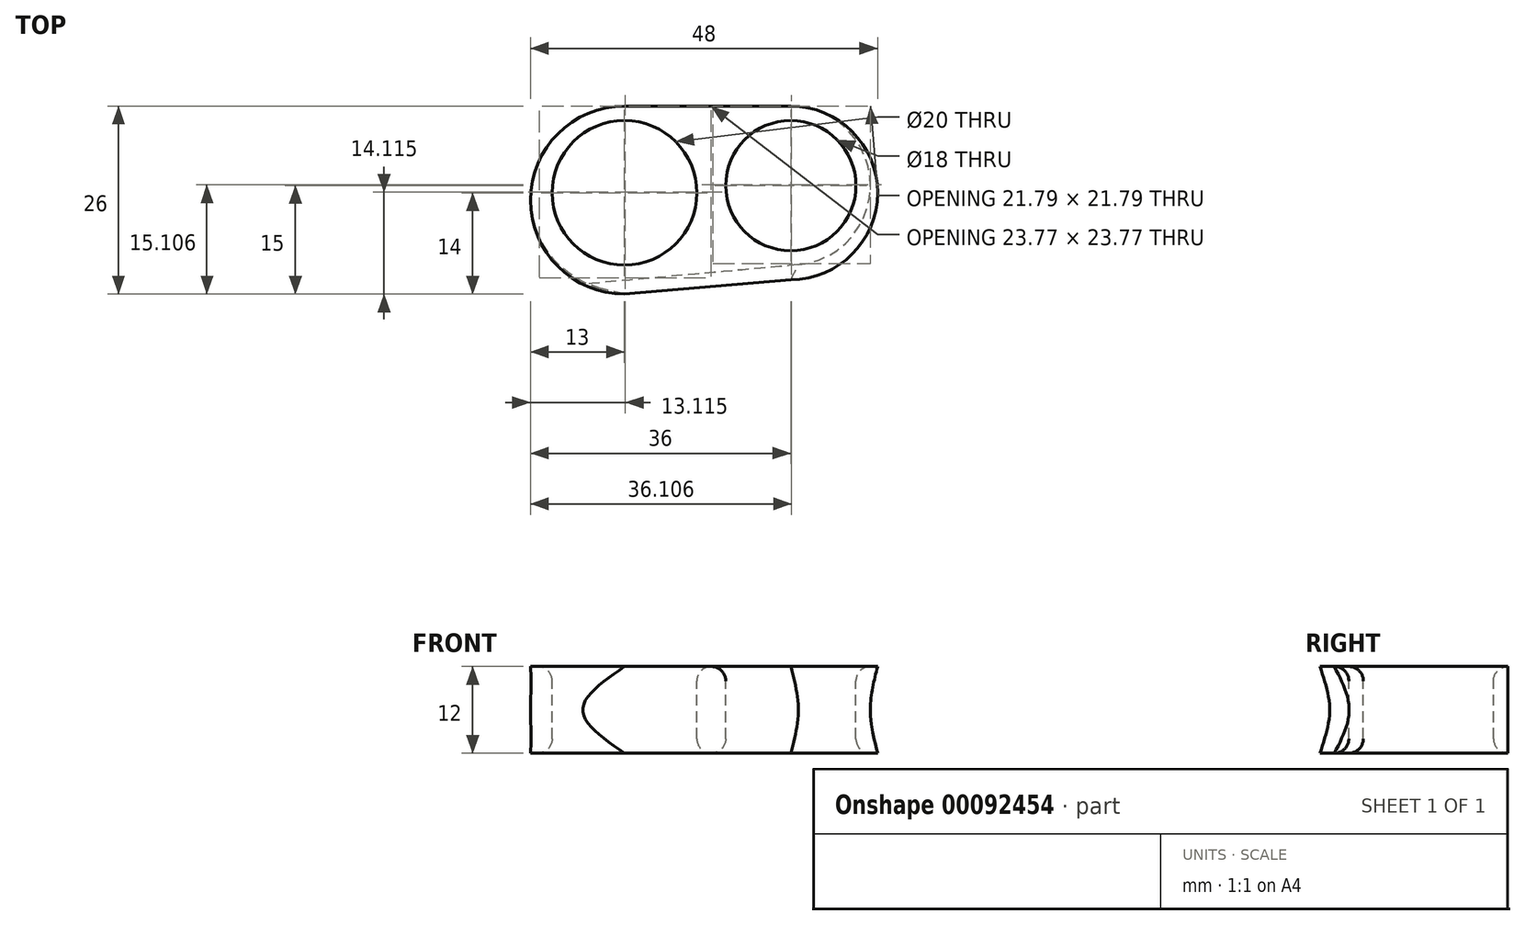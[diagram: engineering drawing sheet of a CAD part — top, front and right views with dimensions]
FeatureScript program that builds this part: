
annotation { "Feature Type Name" : "Feature", "Feature Type Description" : "" }
export const myFeature = defineFeature(function(context is Context, id is Id, definition is map)
    precondition{}
    {
        {
            var Q0;
            Q0=qCreatedBy(makeId("Top.planeOp"),FACE);
            var sketch = newSketch(context, id + "F0", { "sketchPlane" : qUnion([Q0])});
            skLineSegment(sketch, "E0.bottom", {"start": v(26, 15) * mm, "end": v(-26, 15) * mm, "construction": true});
            skLineSegment(sketch, "E0.top", {"start": v(26, -15) * mm, "end": v(-26, -15) * mm, "construction": true});
            skLineSegment(sketch, "E0.left", {"start": v(26, 15) * mm, "end": v(26, -15) * mm, "construction": true});
            skLineSegment(sketch, "E0.right", {"start": v(-26, 15) * mm, "end": v(-26, -15) * mm, "construction": true});
            skPoint(sketch, "E0.middle", {"position": v(0, 0) * mm});
            skLineSegment(sketch, "E1", {"start": v(-26, 13) * mm, "end": v(26, 13) * mm, "construction": true});
            skLineSegment(sketch, "E2", {"start": v(-22, 15) * mm, "end": v(-22, -15) * mm, "construction": true});
            skLineSegment(sketch, "E3", {"start": v(-2, 15) * mm, "end": v(-2, -15) * mm, "construction": true});
            skLineSegment(sketch, "E4", {"start": v(2, 15) * mm, "end": v(2, -15) * mm, "construction": true});
            skLineSegment(sketch, "E5", {"start": v(-24, 15) * mm, "end": v(-24, -15) * mm, "construction": true});
            skLineSegment(sketch, "E6", {"start": v(20, 15) * mm, "end": v(20, -15) * mm, "construction": true});
            skLineSegment(sketch, "E7", {"start": v(-22, -7) * mm, "end": v(-2, -7) * mm, "construction": true});
            skLineSegment(sketch, "E8", {"start": v(2, -5) * mm, "end": v(20, -5) * mm, "construction": true});
            skLineSegment(sketch, "E9", {"start": v(-22, 3) * mm, "end": v(-2, 3) * mm, "construction": true});
            skLineSegment(sketch, "E10", {"start": v(2, 4) * mm, "end": v(20, 4) * mm, "construction": true});
            skCircle(sketch, "E11", {"center": v(-12, 3) * mm, "radius": 10 * mm, "construction": true});
            skCircle(sketch, "E12", {"center": v(11, 4) * mm, "radius": 9 * mm, "construction": true});
            skCircle(sketch, "E13", {"center": v(-12, 3) * mm, "radius": 12 * mm, "construction": true});
            skCircle(sketch, "E14", {"center": v(11, 4) * mm, "radius": 11 * mm, "construction": true});
            skLineSegment(sketch, "E15", {"start": v(-22, -11) * mm, "end": v(-2, -11) * mm, "construction": true});
            skLineSegment(sketch, "E16", {"start": v(2, -9) * mm, "end": v(20, -9) * mm, "construction": true});
            skLineSegment(sketch, "E17", {"start": v(-12, 15) * mm, "end": v(11, 15) * mm, "construction": true});
            skLineSegment(sketch, "E18", {"start": v(-10.96, -8.95) * mm, "end": v(11.95, -6.96) * mm, "construction": true});
            skLineSegment(sketch, "E19", {"start": v(-12, 15) * mm, "end": v(-12, -11) * mm, "construction": true});
            skLineSegment(sketch, "E20", {"start": v(11, 15) * mm, "end": v(11, -9) * mm, "construction": true});
            skArc(sketch, "E21", {"start": v(-12, 15) * mm, "mid": v(-25, 2) * mm, "end": v(-12, -11) * mm, "construction": true});
            skArc(sketch, "E22", {"start": v(11, 15) * mm, "mid": v(23, 3) * mm, "end": v(11, -9) * mm});
            skLineSegment(sketch, "E23", {"start": v(-12, -11) * mm, "end": v(11, -9) * mm});
            skSolve(sketch);
        }
        {
            var Q0;
            Q0=qCreatedBy(makeId("Top.planeOp"),FACE);
            var sketch = newSketch(context, id + "F1", { "sketchPlane" : qUnion([Q0])});
            skLineSegment(sketch, "E24.0", {"start": v(-12, 15) * mm, "end": v(11, 15) * mm});
            skPoint(sketch, "E25", {"position": v(-12, 2) * mm});
            skPoint(sketch, "E26", {"position": v(11, 3) * mm});
            skArc(sketch, "E27", {"start": v(-12, 15) * mm, "mid": v(-25, 2) * mm, "end": v(-12, -11) * mm});
            skArc(sketch, "E28", {"start": v(11, 15) * mm, "mid": v(23, 3) * mm, "end": v(11, -9) * mm});
            skLineSegment(sketch, "E29", {"start": v(-12, -11) * mm, "end": v(11, -9) * mm});
            skSolve(sketch);
        }
        {
            var Q0;
            Q0=qCreatedBy(makeId("Top.planeOp"),FACE);
            cPlane(context, id + "F2", {"entities" : qUnion([Q0]), "cplaneType" : CPlaneType.OFFSET, "offset" : 6 * mm, "width" : 150 * mm, "height" : 150 * mm});
        }
        {
            var Q0;
            Q0=qCreatedBy(id+"F2.planeOp",FACE);
            var sketch = newSketch(context, id + "F3", { "sketchPlane" : qUnion([Q0])});
            skLineSegment(sketch, "E30.0", {"start": v(-12, 15) * mm, "end": v(11, 15) * mm});
            skPoint(sketch, "E31", {"position": v(11, 4) * mm});
            skPoint(sketch, "E32", {"position": v(-12, 2) * mm});
            skLineSegment(sketch, "E33", {"start": v(12.04, -6.95) * mm, "end": v(-17.78, -9.65) * mm});
            skArc(sketch, "E34", {"start": v(-12, 15) * mm, "mid": v(-24.66, 4.97) * mm, "end": v(-17.78, -9.65) * mm});
            skArc(sketch, "E35", {"start": v(11, 15) * mm, "mid": v(21.99, 4.52) * mm, "end": v(12.04, -6.95) * mm});
            skSolve(sketch);
        }
        {
            var Q0;
            Q0=qCreatedBy(id+"F2.planeOp",FACE);
            cPlane(context, id + "F4", {"entities" : qUnion([Q0]), "cplaneType" : CPlaneType.OFFSET, "offset" : 6 * mm, "width" : 150 * mm, "height" : 150 * mm});
        }
        {
            var Q0;
            Q0=qCreatedBy(id+"F4.planeOp",FACE);
            var sketch = newSketch(context, id + "F5", { "sketchPlane" : qUnion([Q0])});
            skLineSegment(sketch, "E36.0", {"start": v(-12, -11) * mm, "end": v(11, -9) * mm});
            skPoint(sketch, "E37", {"position": v(11, 3) * mm});
            skPoint(sketch, "E38", {"position": v(-12, 2) * mm});
            skArc(sketch, "E39", {"start": v(11, 15) * mm, "mid": v(23, 3) * mm, "end": v(11, -9) * mm});
            skArc(sketch, "E40", {"start": v(-12, 15) * mm, "mid": v(-25, 2) * mm, "end": v(-12, -11) * mm});
            skLineSegment(sketch, "E41", {"start": v(-12, 15) * mm, "end": v(11, 15) * mm});
            skSolve(sketch);
        }
        {
            var Q0;
            Q0 = qSketchRegion(id + "F1", true);
            var Q1;
            Q1 = qSketchRegion(id + "F3", true);
            var Q2;
            Q2 = qSketchRegion(id + "F5", true);
            loft(context, id + "F6", {"sheetProfilesArray" : [{ "sheetProfileEntities" : qUnion([Q0]) }, { "sheetProfileEntities" : qUnion([Q1]) }, { "sheetProfileEntities" : qUnion([Q2]) }]});
        }
        {
            var Q0;
            Q0=qCreatedBy(id+"F4.planeOp",FACE);
            var sketch = newSketch(context, id + "F7", { "sketchPlane" : qUnion([Q0])});
            skPoint(sketch, "E42.0", {"position": v(-12, 3) * mm});
            skPoint(sketch, "E43.0", {"position": v(11, 4) * mm});
            skCircle(sketch, "E44", {"center": v(-12, 3) * mm, "radius": 10 * mm});
            skCircle(sketch, "E45", {"center": v(11, 4) * mm, "radius": 9 * mm});
            skSolve(sketch);
        }
        {
            var Q0;
            Q0=makeQuery(id+"F7.imprint","IMPRINT",FACE,{"disambiguationData":[TD([[makeQuery(id+"F7.imprint","IMPRINT",EDGE,{"derivedFrom":sQuery(id+"F7.wireOp",EDGE,"E45")}),1.0]])]});
            var Q1;
            Q1=makeQuery(id+"F7.imprint","IMPRINT",FACE,{"disambiguationData":[TD([[makeQuery(id+"F7.imprint","IMPRINT",EDGE,{"derivedFrom":sQuery(id+"F7.wireOp",EDGE,"E44")}),1.0]])]});
            extrude(context, id + "F8", {"entities" : qUnion([Q0, Q1]), "operationType" : NewBodyOperationType.REMOVE, "oppositeDirection" : true, "depth" : 25 * mm});
        }
        {
            var Q0;
            Q0=makeQuery(id+"F8.boolean.opBoolean","COPY",FACE,{"derivedFrom":makeQuery(id+"F8.opExtrude","SWEPT_FACE",FACE,{"disambiguationData":[OSD([sQuery(id+"F7.wireOp",EDGE,"E44")])]})});
            var Q1;
            Q1=makeQuery(id+"F8.boolean.opBoolean","COPY",FACE,{"derivedFrom":makeQuery(id+"F8.opExtrude","SWEPT_FACE",FACE,{"disambiguationData":[OSD([sQuery(id+"F7.wireOp",EDGE,"E45")])]})});
            fillet(context, id + "F9", {"entities" : qUnion([Q0, Q1]), "radius" : 2 * mm, "tangentPropagation" : true, "allowEdgeOverflow" : false});
        }
    });
